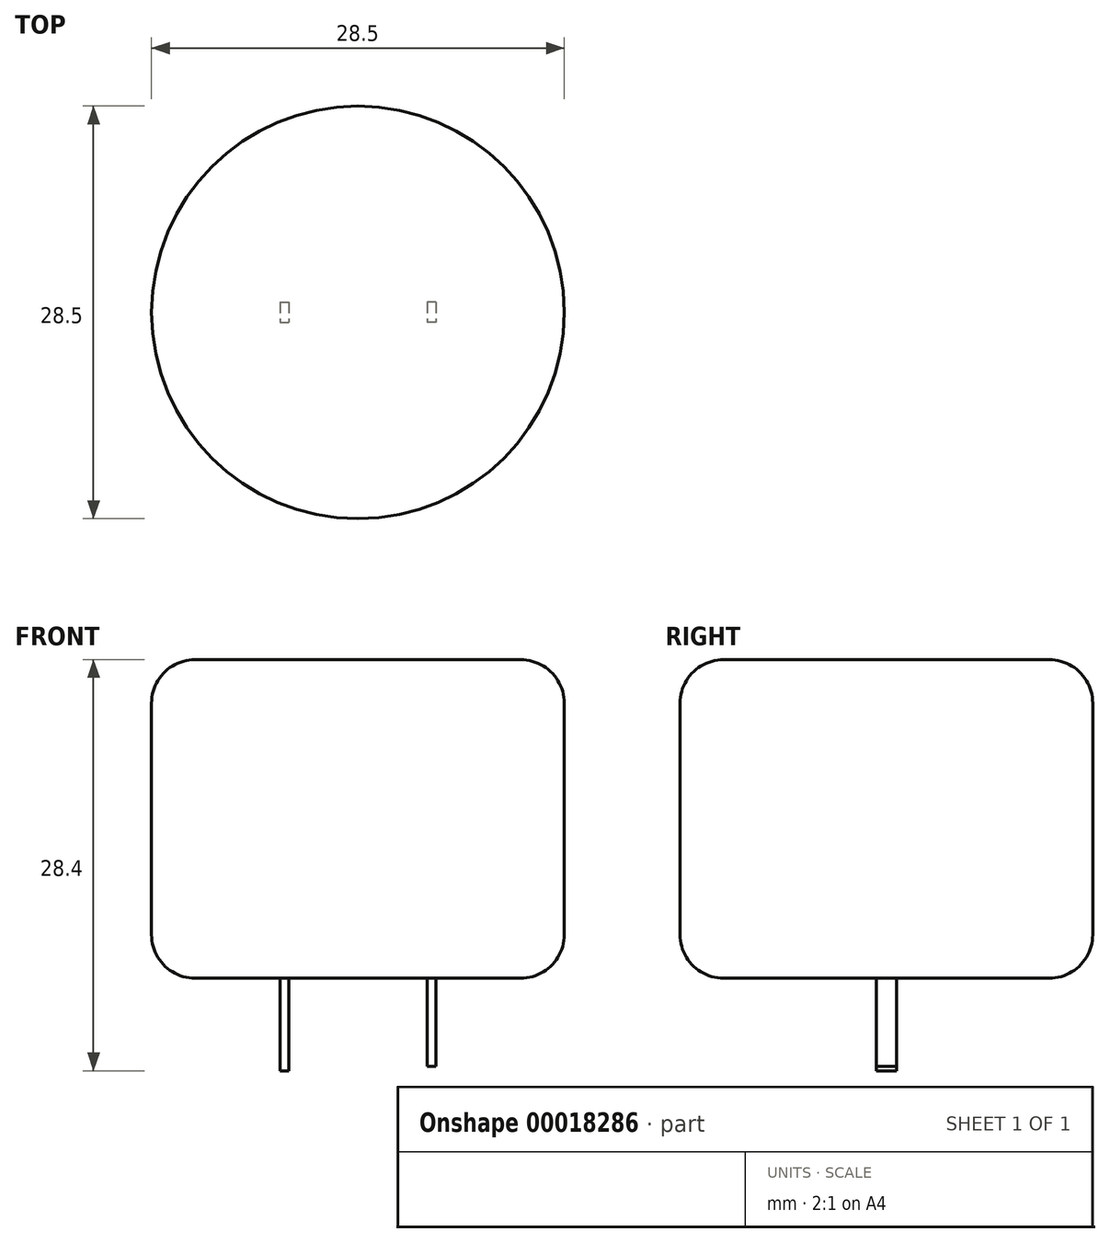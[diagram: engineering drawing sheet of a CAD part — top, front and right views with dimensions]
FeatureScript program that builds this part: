
annotation { "Feature Type Name" : "Feature", "Feature Type Description" : "" }
export const myFeature = defineFeature(function(context is Context, id is Id, definition is map)
    precondition{}
    {
        {
            var Q0;
            Q0=qCreatedBy(makeId("Top.planeOp"),FACE);
            var sketch = newSketch(context, id + "F0", { "sketchPlane" : qUnion([Q0])});
            skCircle(sketch, "E0", {"center": v(0, 0) * mm, "radius": 14.25 * mm});
            skSolve(sketch);
        }
        {
            var Q0;
            Q0 = qSketchRegion(id + "F0", true);
            extrude(context, id + "F1", {"entities" : qUnion([Q0]), "depth" : 22 * mm});
        }
        {
            var Q0;
            Q0=qCreatedBy(makeId("Top.planeOp"),FACE);
            var sketch = newSketch(context, id + "F2", { "sketchPlane" : qUnion([Q0])});
            skLineSegment(sketch, "E1.rect.bottom", {"start": v(5.38, 0.7) * mm, "end": v(4.78, 0.7) * mm});
            skLineSegment(sketch, "E1.rect.top", {"start": v(5.38, -0.7) * mm, "end": v(4.78, -0.7) * mm});
            skLineSegment(sketch, "E1.rect.left", {"start": v(5.38, 0.7) * mm, "end": v(5.38, -0.7) * mm});
            skLineSegment(sketch, "E1.rect.right", {"start": v(4.78, 0.7) * mm, "end": v(4.78, -0.7) * mm});
            skPoint(sketch, "E1.rect.middle", {"position": v(5.08, 0) * mm});
            skLineSegment(sketch, "E2", {"start": v(0, -4.91) * mm, "end": v(0, 5.45) * mm, "construction": true});
            skPoint(sketch, "E3.MirrorP", {"position": v(-5.08, 0) * mm});
            skLineSegment(sketch, "E4.MirrorCS", {"start": v(-5.38, 0.7) * mm, "end": v(-4.78, 0.7) * mm});
            skLineSegment(sketch, "E5.MirrorCS", {"start": v(-5.38, -0.7) * mm, "end": v(-4.78, -0.7) * mm});
            skLineSegment(sketch, "E6.MirrorCS", {"start": v(-5.38, 0.7) * mm, "end": v(-5.38, -0.7) * mm});
            skLineSegment(sketch, "E7.MirrorCS", {"start": v(-4.78, 0.7) * mm, "end": v(-4.78, -0.7) * mm});
            skSolve(sketch);
        }
        {
            var Q0;
            Q0 = qSketchRegion(id + "F2", true);
            extrude(context, id + "F3", {"entities" : qUnion([Q0]), "oppositeDirection" : true, "depth" : 6.1 * mm});
        }
        {
            var Q0;
            Q0=makeQuery(id+"F3.opExtrude","CAP_FACE",FACE,{"disambiguationData":[OSD([sQuery(id+"F2.wireOp",EDGE,"E4.MirrorCS"),sQuery(id+"F2.wireOp",EDGE,"E5.MirrorCS"),sQuery(id+"F2.wireOp",EDGE,"E6.MirrorCS"),sQuery(id+"F2.wireOp",EDGE,"E7.MirrorCS")])],"isStart":false});
            extrude(context, id + "F4", {"entities" : qUnion([Q0]), "operationType" : NewBodyOperationType.ADD, "depth" : 0.3 * mm});
        }
        {
            var Q0;
            Q0=makeQuery(id+"F1.opExtrude","CAP_EDGE",EDGE,{"disambiguationData":[OSD([sQuery(id+"F0.wireOp",EDGE,"E0")])],"isStart":true});
            var Q1;
            Q1=makeQuery(id+"F1.opExtrude","CAP_EDGE",EDGE,{"disambiguationData":[OSD([sQuery(id+"F0.wireOp",EDGE,"E0")])],"isStart":false});
            fillet(context, id + "F5", {"entities" : qUnion([Q0, Q1]), "radius" : 3 * mm, "tangentPropagation" : true, "allowEdgeOverflow" : false});
        }
    });
